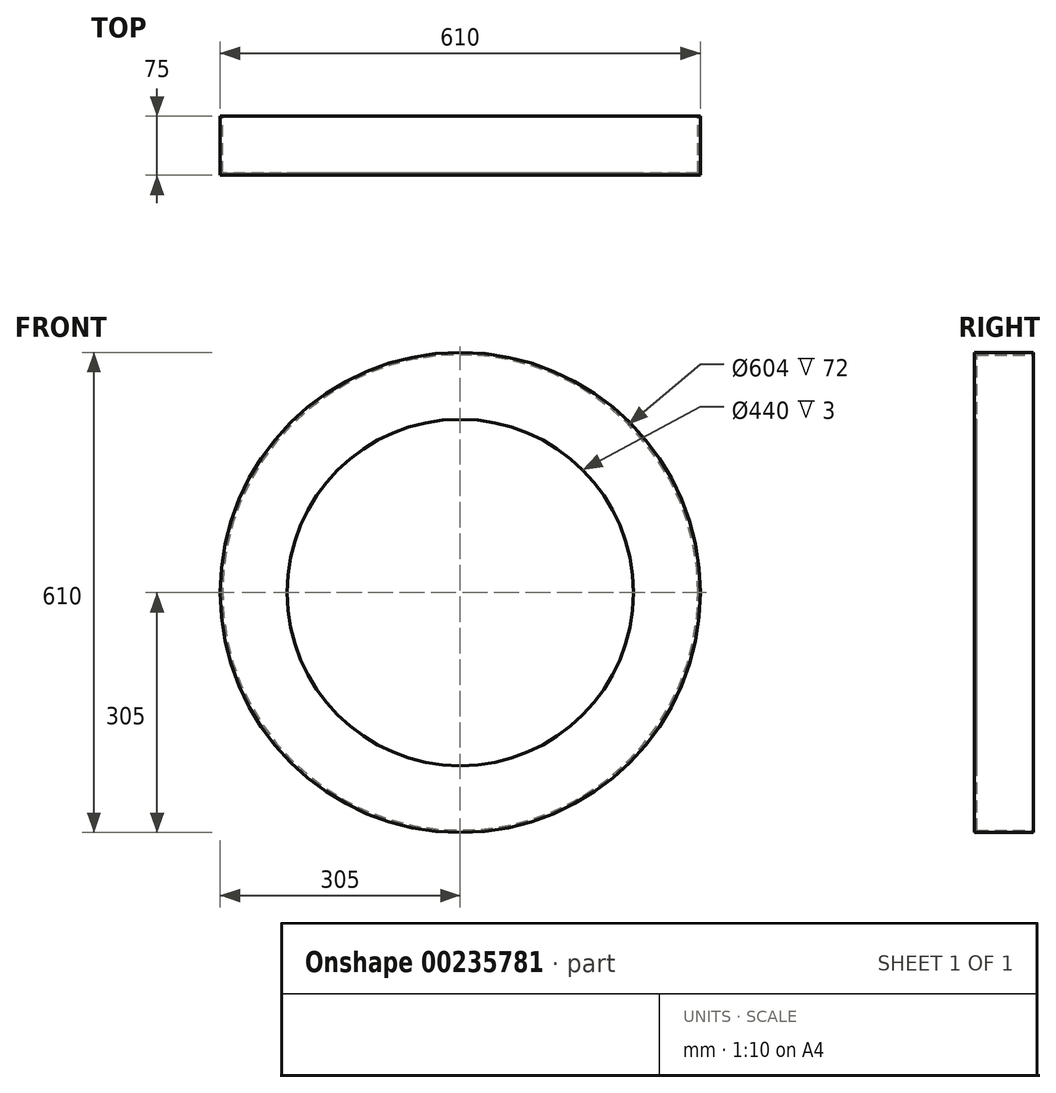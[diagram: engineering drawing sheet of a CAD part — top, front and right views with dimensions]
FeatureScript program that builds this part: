
annotation { "Feature Type Name" : "Feature", "Feature Type Description" : "" }
export const myFeature = defineFeature(function(context is Context, id is Id, definition is map)
    precondition{}
    {
        {
            var Q0;
            Q0=qCreatedBy(makeId("Front.planeOp"),FACE);
            var sketch = newSketch(context, id + "F0", { "sketchPlane" : qUnion([Q0])});
            skCircle(sketch, "E0", {"center": v(0, 0) * mm, "radius": 305 * mm});
            skSolve(sketch);
        }
        {
            var Q0;
            Q0=makeQuery(id+"F0.imprint","IMPRINT",FACE,{"disambiguationData":[TD([[makeQuery(id+"F0.imprint","IMPRINT",EDGE,{"derivedFrom":sQuery(id+"F0.wireOp",EDGE,"E0")}),1.0]])]});
            extrude(context, id + "F1", {"entities" : qUnion([Q0]), "depth" : 75 * mm});
        }
        {
            var Q0;
            Q0=makeQuery(id+"F1.opExtrude","CAP_FACE",FACE,{"disambiguationData":[OSD([sQuery(id+"F0.wireOp",EDGE,"E0")])],"isStart":true});
            shell(context, id + "F2", {"entities" : qUnion([Q0]), "thickness" : 3 * mm});
        }
        {
            var Q0;
            Q0=makeQuery(id+"F1.opExtrude","CAP_FACE",FACE,{"disambiguationData":[OSD([sQuery(id+"F0.wireOp",EDGE,"E0")])],"isStart":false});
            var sketch = newSketch(context, id + "F3", { "sketchPlane" : qUnion([Q0])});
            skCircle(sketch, "E1", {"center": v(0, 0) * mm, "radius": 220 * mm});
            skSolve(sketch);
        }
        {
            var Q0;
            Q0=makeQuery(id+"F3.imprint","IMPRINT",FACE,{"disambiguationData":[TD([[makeQuery(id+"F3.imprint","IMPRINT",EDGE,{"derivedFrom":sQuery(id+"F3.wireOp",EDGE,"E1")}),1.0]])]});
            extrude(context, id + "F4", {"entities" : qUnion([Q0]), "operationType" : NewBodyOperationType.REMOVE, "endBound" : BoundingType.THROUGH_ALL, "oppositeDirection" : true, "depth" : 25 * mm});
        }
    });
